# Revit family: LAMP_KOMBIC 150 SURFACE 2000 CRI80 OPTIC
name_source: partatom
category: Luminarias
revit_build: Autodesk Revit 2018 (Build: 20190510_1515(x64)
units: mm (PartAtom-declared; Revit-internal decimal feet)

## family parameters
Anfitrión = Cara
Compartido = No
Corte con vacíos al cargar = No
Cota de conector redondo = Diámetro de uso
Origen de luz = Sí
Punto de cálculo de habitación = No
Tipo de pieza = Normal

## types (12) — shared parameters
CRI = 80
Cambio de temperatura de color de luz atenuada = <Ninguno>
Diameter = 150 mm
Elevación por defecto = 1219 mm
Fabricante = LAMP
Filtro de color = 16777215
Gear = Electronic
Height = 180 mm  [stored 0.590551 ft]
IEE = A+
Installation instructions = https://www.lamp.es
Insulation class = II
LED Lifetime = 50.000 L90 B10
Lamp = COB LED
Last update = 07/10/2021
Luminaire type = Suspended
MacAdam = 3
Manufacturer URL = http://www.lamp.es
Manufacturer country = Spain
Manufacturer name = LAMP
Material cable suspension = LAMP_Acero genérico
Material difusor = LAMP_PMMA Difusor Kombic
Model explanation = Possibility of chossing between surface or suspended within the model
Plum = 14 W
Power = 12 W
Power Supply = 220-240V 50/60Hz
Product URL = https://www.lamp.es
Product datasheet = http://www.lamp.es
Protection rating = IP40
Type = COB PHILIPS
UGR = 16
Weight = 1.74 kg
Ángulo de inclinación = -90.00°

## per-type parameters (varying)
| type | Archivo de red fotométrica | Efficacy | Finish | Material cuerpo | Material floron | Material reflector | Modelo | Product code |
| 1145LM 3000K  B/B | K21SF2040WF830NBB.IES | 81 lm/W | Matte black RAL 9011 | LAMP_Plástico genérico NG | LAMP_Plástico genérico NG | LAMP_PC Reflector Kombic Metalizado Negro | K21SF2040WF830NBB | K21SF2040WF830NBB |
| 1145LM 3000K  B/W | K21SF2040WF830NBW.IES | 81 lm/W | Matte white RAL 9010 | LAMP_Plástico genérico BL | LAMP_Plástico genérico BL | LAMP_PC Reflector Kombic Metalizado Negro | K21SF2040WF830NBW | K21SF2040WF830NBW |
| 1148LM 3000K  M/B | K21SF2040WF830NMB.IES | 81 lm/W | Matte black RAL 9011 | LAMP_Plástico genérico NG | LAMP_Plástico genérico NG | LAMP_PC Reflector Kombic Metalizado Mate | K21SF2040WF830NMB | K21SF2040WF830NMB |
| 1148LM 3000K  M/W | K21SF2040WF830NMW.IES | 81 lm/W | Matte white RAL 9010 | LAMP_Plástico genérico BL | LAMP_Plástico genérico BL | LAMP_PC Reflector Kombic Metalizado Mate | K21SF2040WF830NMW | K21SF2040WF830NMW |
| 1184LM 3000K  W/B | K21SF2040WF830NWB.IES | 84 lm/W | Matte black RAL 9011 | LAMP_Plástico genérico NG | LAMP_Plástico genérico NG | LAMP_PC Reflector Kombic Blanco | K21SF2040WF830NWB | K21SF2040WF830NWB |
| 1184LM 3000K  W/W | K21SF2040WF830NWW.IES | 84 lm/W | Matte white RAL 9010 | LAMP_Plástico genérico BL | LAMP_Plástico genérico BL | LAMP_PC Reflector Kombic Blanco | K21SF2040WF830NWW | K21SF2040WF830NWW |
| 1193LM 4000K  B/B | K21SF2040WF840NBB.IES | 85 lm/W | Matte black RAL 9011 | LAMP_Plástico genérico NG | LAMP_Plástico genérico NG | LAMP_PC Reflector Kombic Metalizado Negro | K21SF2040WF840NBB | K21SF2040WF840NBB |
| 1193LM 4000K  B/W | K21SF2040WF840NBW.IES | 85 lm/W | Matte white RAL 9010 | LAMP_Plástico genérico BL | LAMP_Plástico genérico BL | LAMP_PC Reflector Kombic Metalizado Negro | K21SF2040WF840NBW | K21SF2040WF840NBW |
| 1196LM 4000K  M/B | K21SF2040WF840NMB.IES | 85 lm/W | Matte black RAL 9011 | LAMP_Plástico genérico NG | LAMP_Plástico genérico NG | LAMP_PC Reflector Kombic Metalizado Mate | K21SF2040WF840NMB | K21SF2040WF840NMB |
| 1196LM 4000K  M/W | K21SF2040WF840NMW.IES | 85 lm/W | Matte white RAL 9010 | LAMP_Plástico genérico BL | LAMP_Plástico genérico BL | LAMP_PC Reflector Kombic Metalizado Mate | K21SF2040WF840NMW | K21SF2040WF840NMW |
| 1233LM 4000K  W/B | K21SF2040WF840NWB.IES | 88 lm/W | Matte black RAL 9011 | LAMP_Plástico genérico NG | LAMP_Plástico genérico NG | LAMP_PC Reflector Kombic Blanco | K21SF2040WF840NWB | K21SF2040WF840NWB |
| 1233LM 4000K  W/W | K21SF2040WF840NWW.IES | 88 lm/W | Matte white RAL 9010 | LAMP_Plástico genérico BL | LAMP_Plástico genérico BL | LAMP_PC Reflector Kombic Blanco | K21SF2040WF840NWW | K21SF2040WF840NWW |

note: [stored X ft] marks values corroborated as IEEE doubles in the binary element streams (Revit-internal decimal feet)
